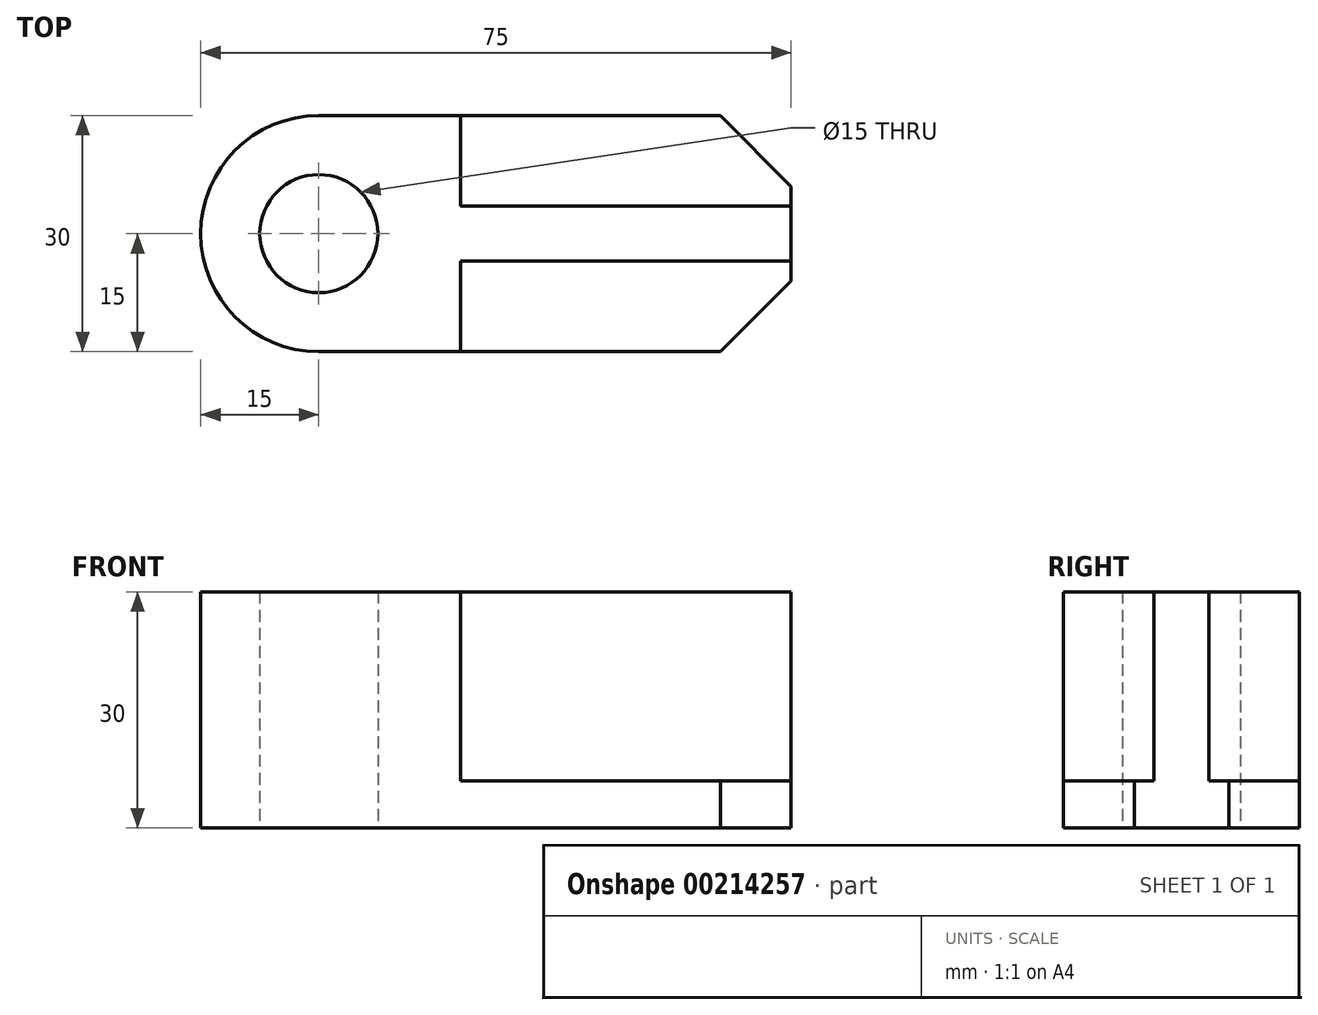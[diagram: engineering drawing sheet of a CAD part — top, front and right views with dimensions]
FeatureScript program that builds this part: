
annotation { "Feature Type Name" : "Feature", "Feature Type Description" : "" }
export const myFeature = defineFeature(function(context is Context, id is Id, definition is map)
    precondition{}
    {
        {
            var Q0;
            Q0=qCreatedBy(makeId("Top.planeOp"),FACE);
            var sketch = newSketch(context, id + "F0", { "sketchPlane" : qUnion([Q0])});
            skLineSegment(sketch, "E0", {"start": v(0, 0) * mm, "end": v(60, 0) * mm, "construction": true});
            skCircle(sketch, "E1", {"center": v(0, 0) * mm, "radius": 7.5 * mm});
            skLineSegment(sketch, "E2", {"start": v(0, -15) * mm, "end": v(0, 15) * mm, "construction": true});
            skArc(sketch, "E3", {"start": v(0, 15) * mm, "mid": v(-15, 0) * mm, "end": v(0, -15) * mm});
            skLineSegment(sketch, "E4", {"start": v(0, 15) * mm, "end": v(18, 15) * mm});
            skLineSegment(sketch, "E5", {"start": v(18, 15) * mm, "end": v(51, 15) * mm});
            skLineSegment(sketch, "E6", {"start": v(51, 15) * mm, "end": v(60, 6) * mm});
            skLineSegment(sketch, "E7", {"start": v(60, 6) * mm, "end": v(60, 0) * mm});
            skLineSegment(sketch, "E8", {"start": v(18, 3.5) * mm, "end": v(18, 15) * mm});
            skLineSegment(sketch, "E9", {"start": v(60, 3.5) * mm, "end": v(18, 3.5) * mm});
            skLineSegment(sketch, "E10.MirrorCS", {"start": v(0, -15) * mm, "end": v(18, -15) * mm});
            skLineSegment(sketch, "E11.MirrorCS", {"start": v(18, -3.5) * mm, "end": v(18, -15) * mm});
            skLineSegment(sketch, "E12.MirrorCS", {"start": v(60, -3.5) * mm, "end": v(18, -3.5) * mm});
            skLineSegment(sketch, "E13.MirrorCS", {"start": v(18, -15) * mm, "end": v(51, -15) * mm});
            skLineSegment(sketch, "E14.MirrorCS", {"start": v(51, -15) * mm, "end": v(60, -6) * mm});
            skLineSegment(sketch, "E15.MirrorCS", {"start": v(60, -6) * mm, "end": v(60, 0) * mm});
            skSolve(sketch);
        }
        {
            var Q0;
            Q0 = qSketchRegion(id + "F0", true);
            extrude(context, id + "F1", {"entities" : qUnion([Q0]), "depth" : 6 * mm});
        }
        {
            var Q0;
            Q0=makeQuery(id+"F0.imprint","IMPRINT",FACE,{"disambiguationData":[TD([[makeQuery(id+"F0.imprint","IMPRINT",EDGE,{"derivedFrom":sQuery(id+"F0.wireOp",EDGE,"E1")}),-1.0]])]});
            extrude(context, id + "F2", {"entities" : qUnion([Q0]), "operationType" : NewBodyOperationType.ADD, "depth" : 30 * mm});
        }
    });
